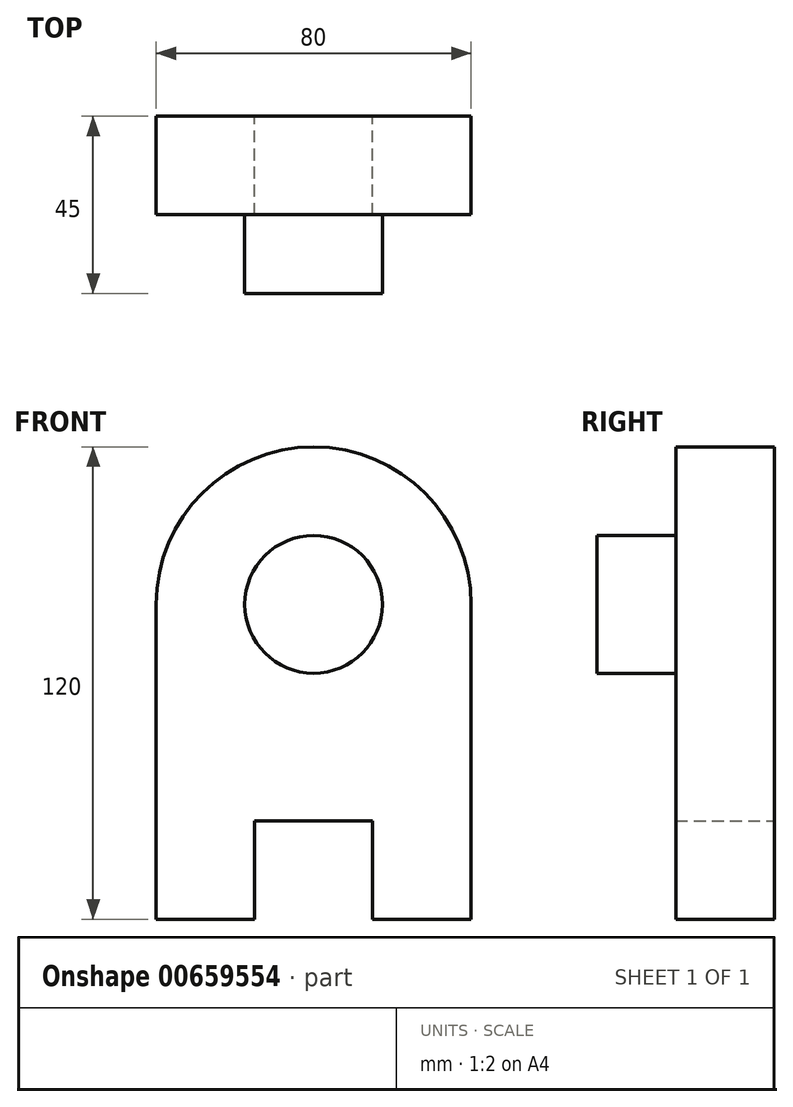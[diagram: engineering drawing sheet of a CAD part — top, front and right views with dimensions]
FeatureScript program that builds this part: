
annotation { "Feature Type Name" : "Feature", "Feature Type Description" : "" }
export const myFeature = defineFeature(function(context is Context, id is Id, definition is map)
    precondition{}
    {
        {
            var Q0;
            Q0=qCreatedBy(makeId("Front.planeOp"),FACE);
            var sketch = newSketch(context, id + "F0", { "sketchPlane" : qUnion([Q0])});
            skLineSegment(sketch, "E0.bottom", {"start": v(-40, -40) * mm, "end": v(-15, -40) * mm});
            skLineSegment(sketch, "E0.left", {"start": v(-40, -40) * mm, "end": v(-40, 40) * mm});
            skLineSegment(sketch, "E0.right", {"start": v(40, -40) * mm, "end": v(40, 40) * mm});
            skPoint(sketch, "E0.middle", {"position": v(0, 0) * mm});
            skArc(sketch, "E1", {"start": v(-40, 40) * mm, "mid": v(0, 80) * mm, "end": v(40, 40) * mm});
            skLineSegment(sketch, "E2", {"start": v(-15, -40) * mm, "end": v(-15, -15) * mm});
            skLineSegment(sketch, "E3", {"start": v(-15, -15) * mm, "end": v(15, -15) * mm});
            skLineSegment(sketch, "E4", {"start": v(15, -15) * mm, "end": v(15, -40) * mm});
            skLineSegment(sketch, "E5", {"start": v(15, -40) * mm, "end": v(40, -40) * mm});
            skCircle(sketch, "E6", {"center": v(0, 40) * mm, "radius": 17.5 * mm});
            skLineSegment(sketch, "E7.trimOffspring", {"start": v(17.5, 40) * mm, "end": v(40, 40) * mm});
            skSolve(sketch);
        }
        {
            var Q0;
            Q0=makeQuery(id+"F0.imprint","IMPRINT",FACE,{"disambiguationData":[TD([[makeQuery(id+"F0.imprint","IMPRINT",EDGE,{"derivedFrom":sQuery(id+"F0.wireOp",EDGE,"E6")}),1.0]])]});
            extrude(context, id + "F1", {"entities" : qUnion([Q0]), "depth" : 45 * mm, "offsetDistance" : 25 * mm});
        }
        {
            var Q0;
            Q0 = qSketchRegion(id + "F0", true);
            extrude(context, id + "F2", {"entities" : qUnion([Q0]), "operationType" : NewBodyOperationType.ADD, "depth" : 25 * mm, "offsetDistance" : 25 * mm});
        }
    });
